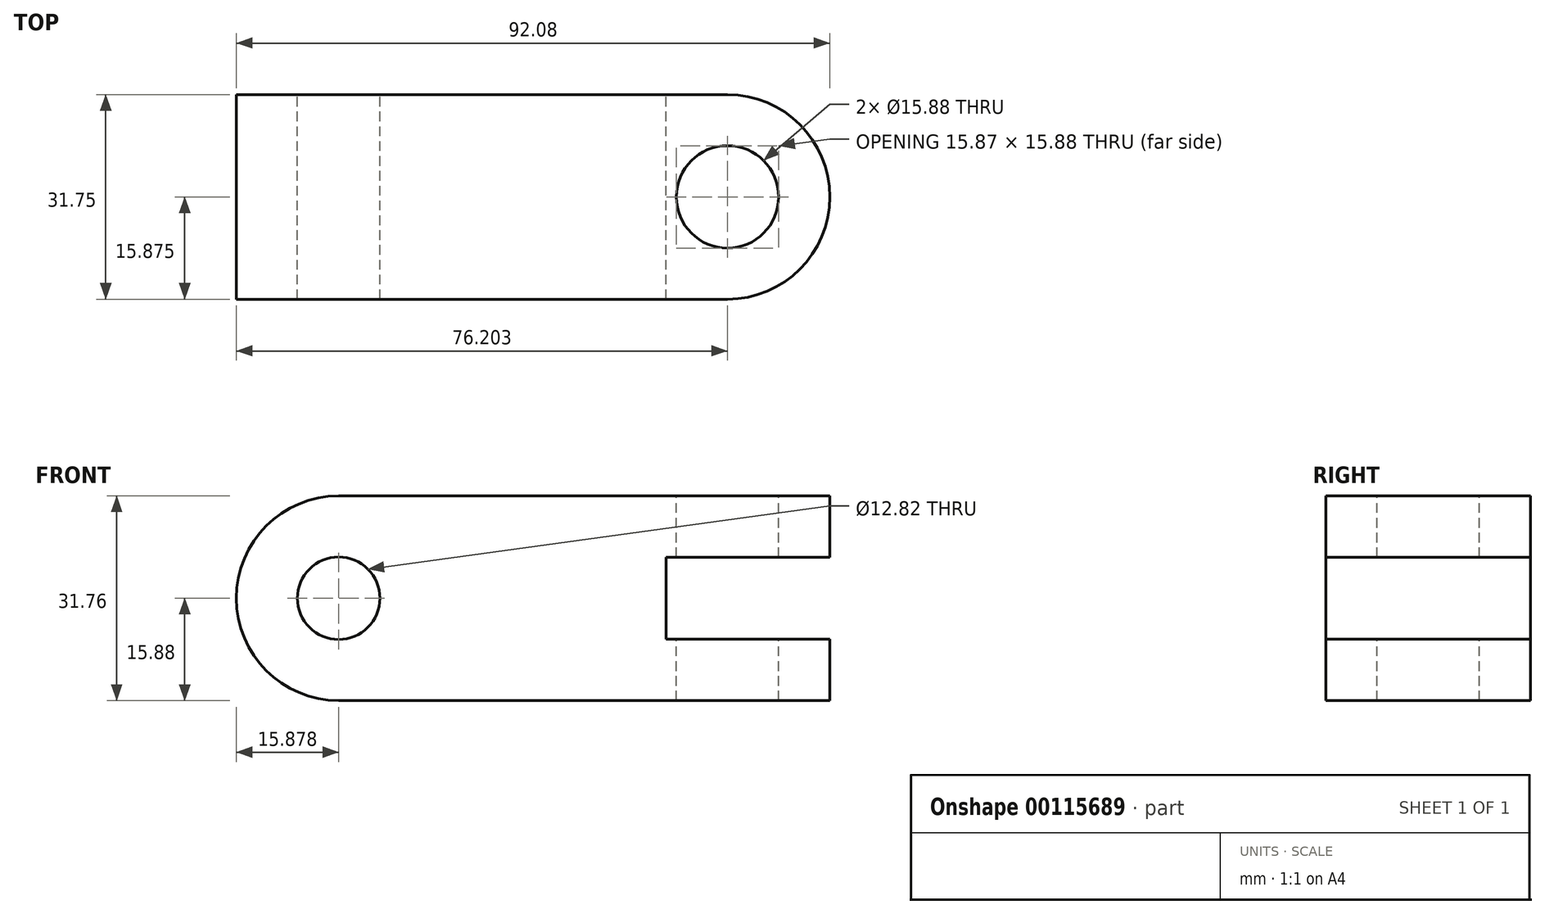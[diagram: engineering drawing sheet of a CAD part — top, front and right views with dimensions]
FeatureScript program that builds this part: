
annotation { "Feature Type Name" : "Feature", "Feature Type Description" : "" }
export const myFeature = defineFeature(function(context is Context, id is Id, definition is map)
    precondition{}
    {
        {
            var Q0;
            Q0=qCreatedBy(makeId("Front.planeOp"),FACE);
            var sketch = newSketch(context, id + "F0", { "sketchPlane" : qUnion([Q0])});
            skLineSegment(sketch, "E0", {"start": v(-43.71, 9.52) * mm, "end": v(32.49, 9.52) * mm});
            skLineSegment(sketch, "E1", {"start": v(32.49, 9.52) * mm, "end": v(32.49, 0) * mm});
            skLineSegment(sketch, "E2", {"start": v(32.49, 0) * mm, "end": v(7.09, 0) * mm});
            skLineSegment(sketch, "E3", {"start": v(7.09, 0) * mm, "end": v(7.09, -12.7) * mm});
            skLineSegment(sketch, "E4", {"start": v(7.09, -12.7) * mm, "end": v(32.49, -12.7) * mm});
            skLineSegment(sketch, "E5", {"start": v(32.49, -12.7) * mm, "end": v(32.49, -22.23) * mm});
            skLineSegment(sketch, "E6", {"start": v(32.49, -22.23) * mm, "end": v(-43.71, -22.23) * mm});
            skArc(sketch, "E7", {"start": v(-43.71, 9.52) * mm, "mid": v(-59.59, -6.35) * mm, "end": v(-43.71, -22.23) * mm});
            skCircle(sketch, "E8", {"center": v(-43.71, -6.35) * mm, "radius": 6.4 * mm});
            skSolve(sketch);
        }
        {
            var Q0;
            Q0=makeQuery(id+"F0.imprint","IMPRINT",FACE,{"disambiguationData":[TD([[makeQuery(id+"F0.imprint","IMPRINT",EDGE,{"derivedFrom":sQuery(id+"F0.wireOp",EDGE,"E0")}),-1.0]])]});
            extrude(context, id + "F1", {"entities" : qUnion([Q0]), "depth" : 31.75 * mm});
        }
        {
            var Q0;
            Q0=makeQuery(id+"F1.opExtrude","SWEPT_FACE",FACE,{"disambiguationData":[OSD([sQuery(id+"F0.wireOp",EDGE,"E0")])]});
            var sketch = newSketch(context, id + "F2", { "sketchPlane" : qUnion([Q0])});
            skLineSegment(sketch, "E9", {"start": v(32.49, -15.88) * mm, "end": v(16.61, -15.88) * mm, "construction": true});
            skCircle(sketch, "E10", {"center": v(16.61, -15.88) * mm, "radius": 7.94 * mm});
            skSolve(sketch);
        }
        {
            var Q0;
            Q0=sQuery(id+"F2.wireOp",VERTEX,"E10.center");
            var Q1;
            Q1=makeQuery(id+"F1.opExtrude","SWEPT_BODY",BODY,{"disambiguationData":[OSD([sQuery(id+"F0.wireOp",EDGE,"E0"),sQuery(id+"F0.wireOp",EDGE,"E1"),sQuery(id+"F0.wireOp",EDGE,"E2"),sQuery(id+"F0.wireOp",EDGE,"E3"),sQuery(id+"F0.wireOp",EDGE,"E4"),sQuery(id+"F0.wireOp",EDGE,"E5"),sQuery(id+"F0.wireOp",EDGE,"E6"),sQuery(id+"F0.wireOp",EDGE,"E7"),sQuery(id+"F0.wireOp",EDGE,"E8")])]});
            hole(context, id + "F3", {"style" : HoleStyle.SIMPLE, "endStyle" : HoleEndStyle.THROUGH, "holeDiameter" : 15.88 * mm, "locations" : qUnion([Q0]), "scope" : qUnion([Q1]), "isTappedThrough" : true});
        }
        {
            var Q0;
            Q0=makeQuery(id+"F1.opExtrude","CAP_EDGE",EDGE,{"disambiguationData":[OSD([sQuery(id+"F0.wireOp",EDGE,"E1")])],"isStart":false});
            var Q1;
            Q1=makeQuery(id+"F1.opExtrude","CAP_EDGE",EDGE,{"disambiguationData":[OSD([sQuery(id+"F0.wireOp",EDGE,"E1")])],"isStart":true});
            var Q2;
            Q2=makeQuery(id+"F1.opExtrude","CAP_EDGE",EDGE,{"disambiguationData":[OSD([sQuery(id+"F0.wireOp",EDGE,"E5")])],"isStart":false});
            var Q3;
            Q3=makeQuery(id+"F1.opExtrude","CAP_EDGE",EDGE,{"disambiguationData":[OSD([sQuery(id+"F0.wireOp",EDGE,"E5")])],"isStart":true});
            fillet(context, id + "F4", {"entities" : qUnion([Q0, Q1, Q2, Q3]), "radius" : 15.88 * mm, "tangentPropagation" : true, "allowEdgeOverflow" : false});
        }
    });
